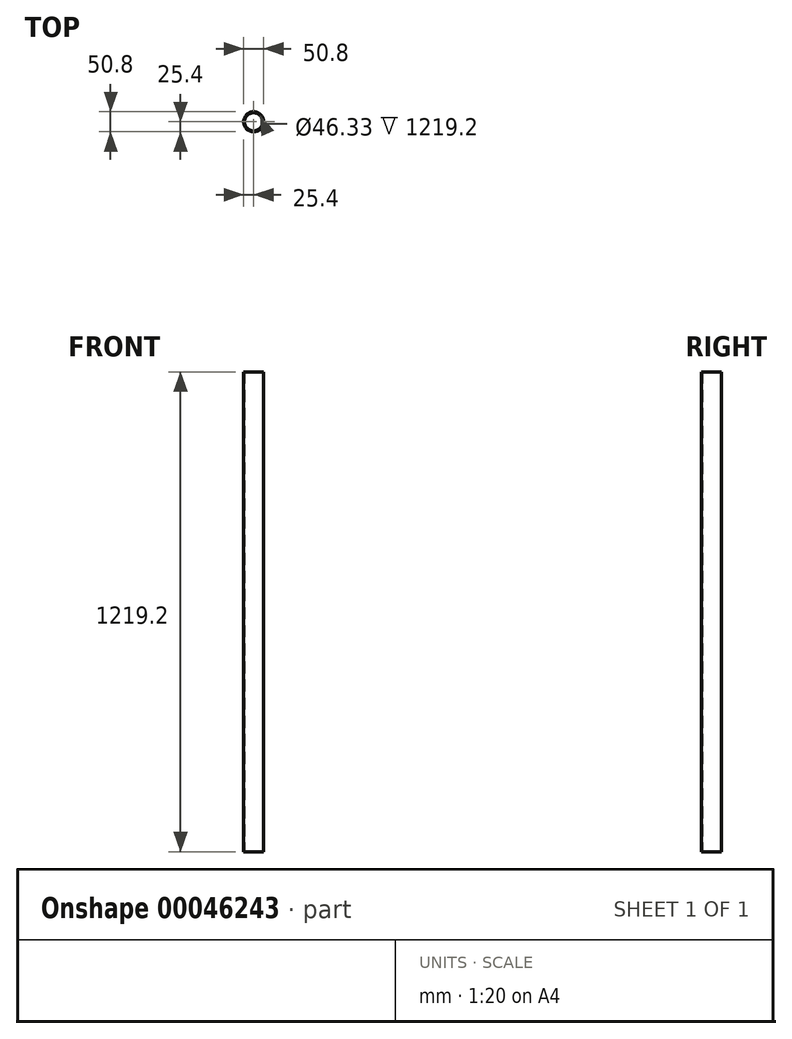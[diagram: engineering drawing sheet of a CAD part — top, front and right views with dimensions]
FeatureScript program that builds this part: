
annotation { "Feature Type Name" : "Feature", "Feature Type Description" : "" }
export const myFeature = defineFeature(function(context is Context, id is Id, definition is map)
    precondition{}
    {
        {
            var Q0;
            Q0=qCreatedBy(makeId("Top.planeOp"),FACE);
            var sketch = newSketch(context, id + "F0", { "sketchPlane" : qUnion([Q0])});
            skCircle(sketch, "E0", {"center": v(0, 0) * mm, "radius": 25.4 * mm});
            skCircle(sketch, "E1", {"center": v(0, 0) * mm, "radius": 23.16 * mm});
            skSolve(sketch);
        }
        {
            var Q0;
            Q0=makeQuery(id+"F0.imprint","IMPRINT",FACE,{"disambiguationData":[TD([[makeQuery(id+"F0.imprint","IMPRINT",EDGE,{"derivedFrom":sQuery(id+"F0.wireOp",EDGE,"E0")}),1.0]])]});
            extrude(context, id + "F1", {"entities" : qUnion([Q0]), "depth" : 1219.2 * mm});
        }
    });
